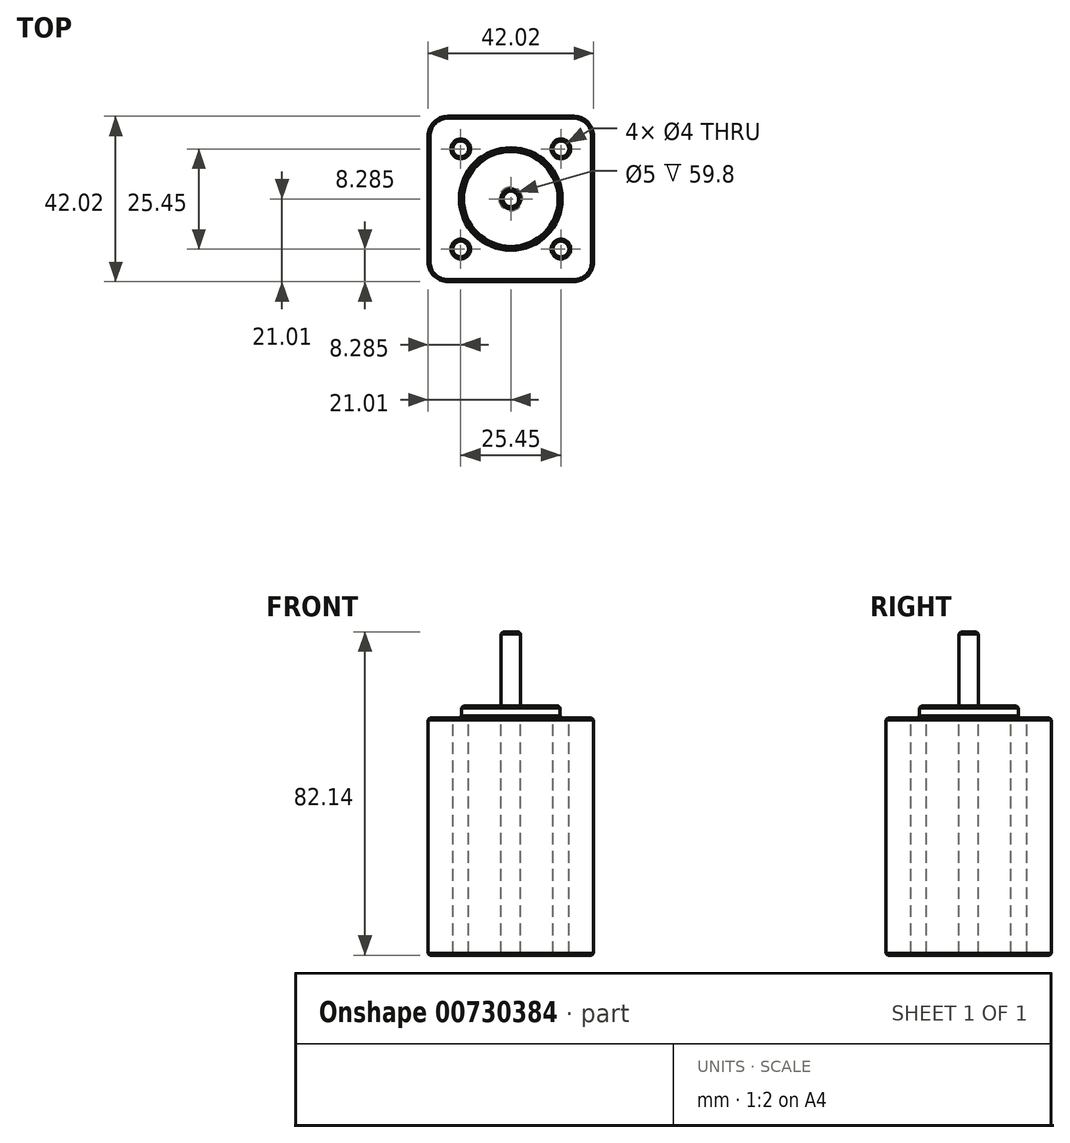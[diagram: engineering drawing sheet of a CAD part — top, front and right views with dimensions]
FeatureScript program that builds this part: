
annotation { "Feature Type Name" : "Feature", "Feature Type Description" : "" }
export const myFeature = defineFeature(function(context is Context, id is Id, definition is map)
    precondition{}
    {
        {
            var Q0;
            Q0=qCreatedBy(makeId("Top.planeOp"),FACE);
            var sketch = newSketch(context, id + "F0", { "sketchPlane" : qUnion([Q0])});
            skLineSegment(sketch, "E0.bottom", {"start": v(16, 21) * mm, "end": v(-16, 21) * mm});
            skLineSegment(sketch, "E0.top", {"start": v(16, -21) * mm, "end": v(-16, -21) * mm});
            skLineSegment(sketch, "E0.left", {"start": v(21, 16) * mm, "end": v(21, -16) * mm});
            skLineSegment(sketch, "E0.right", {"start": v(-21, 16) * mm, "end": v(-21, -16) * mm});
            skPoint(sketch, "E0.middle", {"position": v(0, 0) * mm});
            skCircle(sketch, "E1", {"center": v(0, 0) * mm, "radius": 18 * mm, "construction": true});
            skCircle(sketch, "E2", {"center": v(0, 0) * mm, "radius": 12.55 * mm});
            skCircle(sketch, "E3", {"center": v(0, 0) * mm, "radius": 2.5 * mm});
            skCircle(sketch, "E4", {"center": v(12.73, 12.73) * mm, "radius": 2 * mm});
            skLineSegment(sketch, "E5", {"start": v(0, 0) * mm, "end": v(12.73, 12.73) * mm, "construction": true});
            skCircle(sketch, "E6.1.0", {"center": v(-12.73, 12.73) * mm, "radius": 2 * mm});
            skCircle(sketch, "E6.2.0", {"center": v(-12.73, -12.73) * mm, "radius": 2 * mm});
            skCircle(sketch, "E6.3.0", {"center": v(12.73, -12.73) * mm, "radius": 2 * mm});
            skPoint(sketch, "E7.visualSharp", {"position": v(-21, 21) * mm});
            skArc(sketch, "E7.filletArc", {"start": v(-16, 21) * mm, "mid": v(-19.54, 19.54) * mm, "end": v(-21, 16) * mm});
            skPoint(sketch, "E8.visualSharp", {"position": v(-21, -21) * mm});
            skArc(sketch, "E8.filletArc", {"start": v(-21, -16) * mm, "mid": v(-19.54, -19.54) * mm, "end": v(-16, -21) * mm});
            skPoint(sketch, "E9.visualSharp", {"position": v(21, -21) * mm});
            skArc(sketch, "E9.filletArc", {"start": v(16, -21) * mm, "mid": v(19.54, -19.54) * mm, "end": v(21, -16) * mm});
            skPoint(sketch, "E10.visualSharp", {"position": v(21, 21) * mm});
            skArc(sketch, "E10.filletArc", {"start": v(21, 16) * mm, "mid": v(19.54, 19.54) * mm, "end": v(16, 21) * mm});
            skSolve(sketch);
        }
        {
            var Q0;
            Q0=makeQuery(id+"F0.imprint","IMPRINT",FACE,{"disambiguationData":[TD([[makeQuery(id+"F0.imprint","IMPRINT",EDGE,{"derivedFrom":sQuery(id+"F0.wireOp",EDGE,"E0.bottom")}),1.0]])]});
            var Q1;
            Q1=makeQuery(id+"F0.imprint","IMPRINT",FACE,{"disambiguationData":[TD([[makeQuery(id+"F0.imprint","IMPRINT",EDGE,{"derivedFrom":sQuery(id+"F0.wireOp",EDGE,"E2")}),1.0]])]});
            extrude(context, id + "F1", {"entities" : qUnion([Q0, Q1]), "oppositeDirection" : true, "depth" : 60.3 * mm, "offsetDistance" : 25 * mm});
        }
        {
            var Q0;
            Q0=makeQuery(id+"F0.imprint","IMPRINT",FACE,{"disambiguationData":[TD([[makeQuery(id+"F0.imprint","IMPRINT",EDGE,{"derivedFrom":sQuery(id+"F0.wireOp",EDGE,"E2")}),1.0]])]});
            extrude(context, id + "F2", {"entities" : qUnion([Q0]), "operationType" : NewBodyOperationType.ADD, "depth" : 3.05 * mm, "offsetDistance" : 25 * mm});
        }
        {
            var Q0;
            Q0=makeQuery(id+"F0.imprint","IMPRINT",FACE,{"disambiguationData":[TD([[makeQuery(id+"F0.imprint","IMPRINT",EDGE,{"derivedFrom":sQuery(id+"F0.wireOp",EDGE,"E3")}),1.0]])]});
            extrude(context, id + "F3", {"entities" : qUnion([Q0]), "operationType" : NewBodyOperationType.ADD, "depth" : 21.84 * mm, "offsetDistance" : 25 * mm});
        }
        {
            var Q0;
            Q0=makeQuery(id+"F3.opExtrude","CAP_EDGE",EDGE,{"disambiguationData":[OSD([sQuery(id+"F0.wireOp",EDGE,"E3")])],"isStart":false});
            var Q1;
            Q1=makeQuery(id+"F2.opExtrude","CAP_EDGE",EDGE,{"disambiguationData":[OSD([sQuery(id+"F0.wireOp",EDGE,"E2")])],"isStart":false});
            var Q2;
            Q2=makeQuery(id+"F1.opExtrude","CAP_EDGE",EDGE,{"disambiguationData":[OSD([sQuery(id+"F0.wireOp",EDGE,"E6.2.0")])],"isStart":true});
            var Q3;
            Q3=makeQuery(id+"F1.opExtrude","CAP_EDGE",EDGE,{"disambiguationData":[OSD([sQuery(id+"F0.wireOp",EDGE,"E6.1.0")])],"isStart":true});
            var Q4;
            Q4=makeQuery(id+"F1.opExtrude","CAP_EDGE",EDGE,{"disambiguationData":[OSD([sQuery(id+"F0.wireOp",EDGE,"E4")])],"isStart":true});
            var Q5;
            Q5=makeQuery(id+"F1.opExtrude","CAP_EDGE",EDGE,{"disambiguationData":[OSD([sQuery(id+"F0.wireOp",EDGE,"E6.3.0")])],"isStart":true});
            var Q6;
            Q6=makeQuery(id+"F1.opExtrude","CAP_FACE",FACE,{"disambiguationData":[OSD([sQuery(id+"F0.wireOp",EDGE,"E0.bottom"),sQuery(id+"F0.wireOp",EDGE,"E0.top"),sQuery(id+"F0.wireOp",EDGE,"E0.left"),sQuery(id+"F0.wireOp",EDGE,"E0.right"),sQuery(id+"F0.wireOp",EDGE,"E3"),sQuery(id+"F0.wireOp",EDGE,"E4"),sQuery(id+"F0.wireOp",EDGE,"E6.1.0"),sQuery(id+"F0.wireOp",EDGE,"E6.2.0"),sQuery(id+"F0.wireOp",EDGE,"E6.3.0")])],"isStart":true});
            var Q7;
            Q7=makeQuery(id+"F1.opExtrude","CAP_FACE",FACE,{"disambiguationData":[OSD([sQuery(id+"F0.wireOp",EDGE,"E0.bottom"),sQuery(id+"F0.wireOp",EDGE,"E0.top"),sQuery(id+"F0.wireOp",EDGE,"E0.left"),sQuery(id+"F0.wireOp",EDGE,"E0.right"),sQuery(id+"F0.wireOp",EDGE,"E3"),sQuery(id+"F0.wireOp",EDGE,"E4"),sQuery(id+"F0.wireOp",EDGE,"E6.1.0"),sQuery(id+"F0.wireOp",EDGE,"E6.2.0"),sQuery(id+"F0.wireOp",EDGE,"E6.3.0"),sQuery(id+"F0.wireOp",EDGE,"E7.filletArc"),sQuery(id+"F0.wireOp",EDGE,"E8.filletArc"),sQuery(id+"F0.wireOp",EDGE,"E9.filletArc"),sQuery(id+"F0.wireOp",EDGE,"E10.filletArc")])],"isStart":false});
            chamfer(context, id + "F4", {"entities" : qUnion([Q0, Q1, Q2, Q3, Q4, Q5, Q6, Q7]), "width" : .5 * mm, "tangentPropagation" : true});
        }
    });
